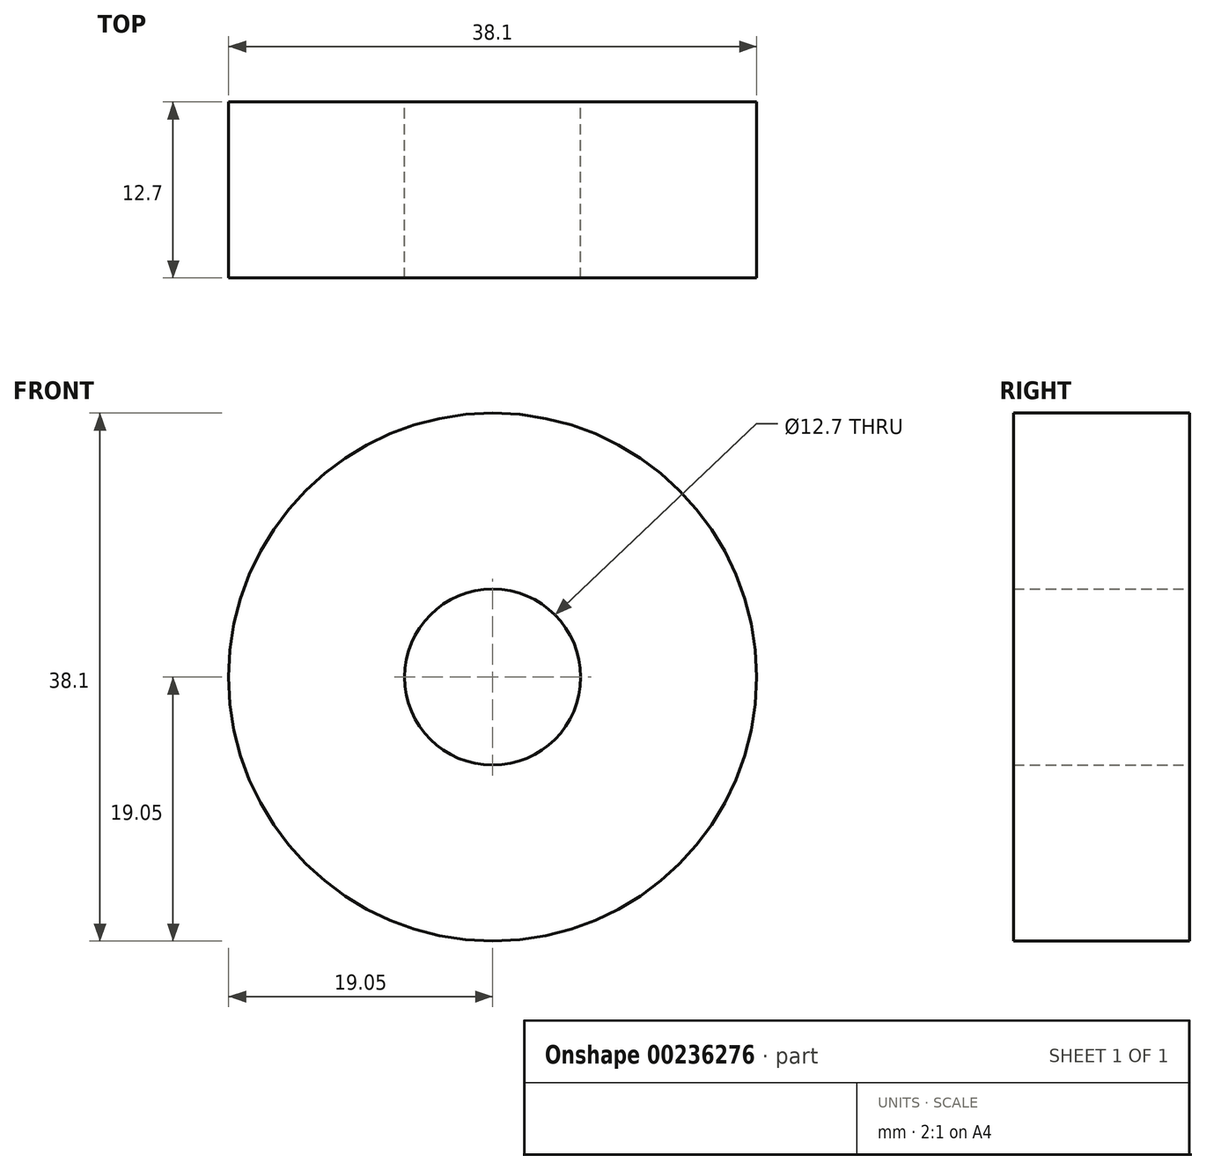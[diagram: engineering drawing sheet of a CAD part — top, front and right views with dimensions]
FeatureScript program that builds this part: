
annotation { "Feature Type Name" : "Feature", "Feature Type Description" : "" }
export const myFeature = defineFeature(function(context is Context, id is Id, definition is map)
    precondition{}
    {
        {
            var Q0;
            Q0=qCreatedBy(makeId("Front.planeOp"),FACE);
            var sketch = newSketch(context, id + "F0", { "sketchPlane" : qUnion([Q0])});
            skCircle(sketch, "E0", {"center": v(0, 0) * mm, "radius": 19.05 * mm});
            skCircle(sketch, "E1", {"center": v(0, 0) * mm, "radius": 6.35 * mm});
            skSolve(sketch);
        }
        {
            var Q0;
            Q0 = qSketchRegion(id + "F0", true);
            extrude(context, id + "F1", {"entities" : qUnion([Q0]), "depth" : 12.7 * mm});
        }
    });
